# Revit family: Haworth_Cloud_Shelf
name_source: partatom
category: Furniture
revit_build: Autodesk Revit 2018 (Build: 20170223_1515(x64)
units: mm (PartAtom-declared; Revit-internal decimal feet)

## family parameters
Always vertical = No
Cut with Voids When Loaded = No
OmniClass Number = 23.40.70.14.64.21.14
OmniClass Title = Free-Standing Component
Room Calculation Point = No
Shared = No
Work Plane-Based = No

## types (1)
- HCCE-CLD
    Actual Depth = 1' - 3 3/4"
    Actual Height = 3' - 5 1/4"
    Actual Width = 6' - 1 3/4"
    Assembly Code = E2020200
    Description = Haworth Cloud Shelf
    Manufacturer = Haworth
    Model = HCCE-CLD
    Revision Number = 4
    Shelf Finish = Haworth _ Polymer _ Snow
    Size = Verify Final Dim. w/ Haworth
    URL = http://www.haworth.com
    URL - Product = https://www.haworth.com
    Void Offset = 0' - 2"
    Warranty = http://www.haworth.com

## geometry (parser evidence)
native form markers: Sweep x2
no freeform markers — native parametric forms only
